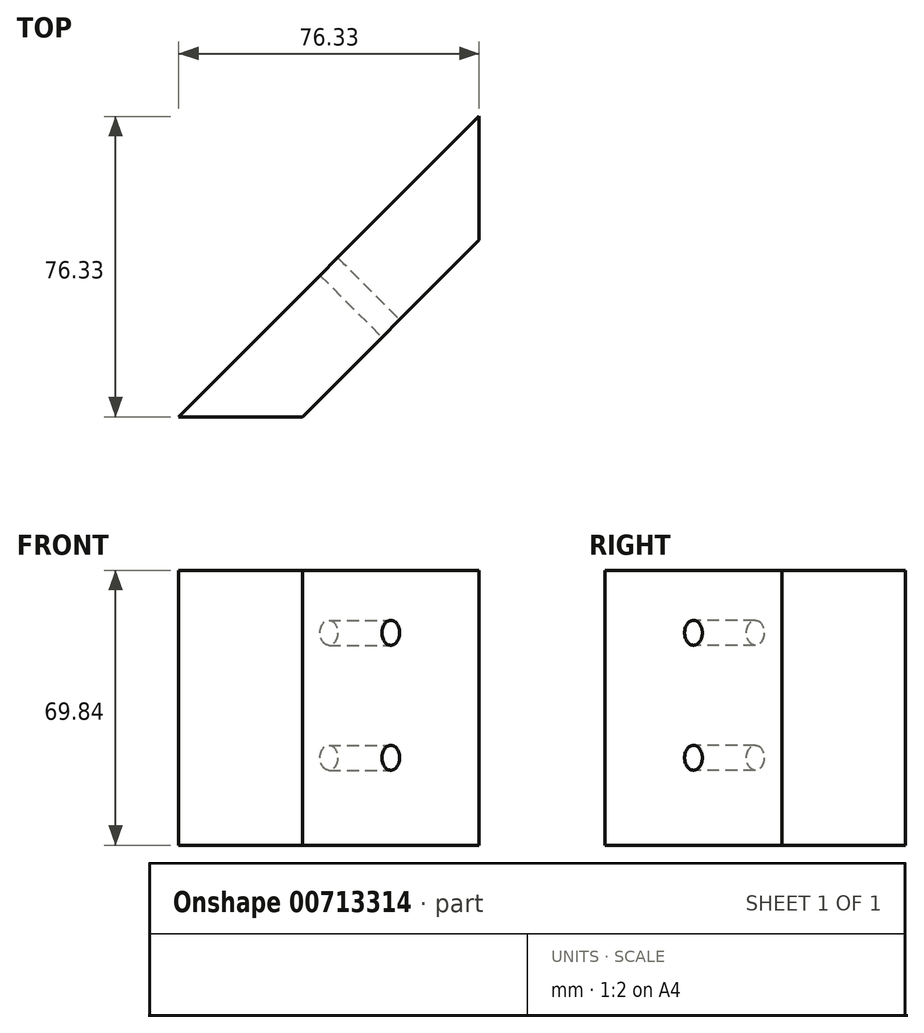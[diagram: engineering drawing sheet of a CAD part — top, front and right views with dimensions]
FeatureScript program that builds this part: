
annotation { "Feature Type Name" : "Feature", "Feature Type Description" : "" }
export const myFeature = defineFeature(function(context is Context, id is Id, definition is map)
    precondition{}
    {
        {
            var Q0;
            Q0=qCreatedBy(makeId("Top.planeOp"),FACE);
            var sketch = newSketch(context, id + "F0", { "sketchPlane" : qUnion([Q0])});
            skLineSegment(sketch, "E0.bottom", {"start": v(-30.3, -46.02) * mm, "end": v(-46.02, -30.3) * mm});
            skLineSegment(sketch, "E0.top", {"start": v(46.02, 30.3) * mm, "end": v(30.3, 46.02) * mm});
            skLineSegment(sketch, "E0.left", {"start": v(-30.3, -46.02) * mm, "end": v(46.02, 30.3) * mm});
            skLineSegment(sketch, "E0.right", {"start": v(-46.02, -30.3) * mm, "end": v(30.3, 46.02) * mm});
            skPoint(sketch, "E0.middle", {"position": v(0, 0) * mm});
            skSolve(sketch);
        }
        {
            var Q0;
            Q0 = qSketchRegion(id + "F0", true);
            extrude(context, id + "F1", {"entities" : qUnion([Q0]), "endBound" : BoundingType.SYMMETRIC, "depth" : 69.85 * mm, "offsetDistance" : 25.4 * mm});
        }
        {
            var Q0;
            Q0=makeQuery(id+"F1.opExtrude","SWEPT_EDGE",EDGE,{"disambiguationData":[OSD([sQuery(id+"F0.wireOp",EDGE,"E0.top"),sQuery(id+"F0.wireOp",EDGE,"E0.left")])]});
            chamfer(context, id + "F2", {"entities" : qUnion([Q0]), "width" : 22.22 * mm, "tangentPropagation" : true});
        }
        {
            var Q0;
            Q0=makeQuery(id+"F1.opExtrude","SWEPT_EDGE",EDGE,{"disambiguationData":[OSD([sQuery(id+"F0.wireOp",EDGE,"E0.bottom"),sQuery(id+"F0.wireOp",EDGE,"E0.left")])]});
            chamfer(context, id + "F3", {"entities" : qUnion([Q0]), "width" : 22.22 * mm, "tangentPropagation" : true});
        }
        {
            var Q0;
            Q0=makeQuery(id+"F1.opExtrude","SWEPT_FACE",FACE,{"disambiguationData":[OSD([sQuery(id+"F0.wireOp",EDGE,"E0.left")])]});
            var sketch = newSketch(context, id + "F4", { "sketchPlane" : qUnion([Q0])});
            skCircle(sketch, "E1", {"center": v(0, 19.05) * mm, "radius": 3.18 * mm});
            skCircle(sketch, "E2", {"center": v(0, -12.7) * mm, "radius": 3.18 * mm});
            skSolve(sketch);
        }
        {
            var Q0;
            Q0=sQuery(id+"F4.wireOp",VERTEX,"E1.center");
            var Q1;
            Q1=makeQuery(id+"F1.opExtrude","SWEPT_BODY",BODY,{"disambiguationData":[OSD([sQuery(id+"F0.wireOp",EDGE,"E0.bottom"),sQuery(id+"F0.wireOp",EDGE,"E0.top"),sQuery(id+"F0.wireOp",EDGE,"E0.left"),sQuery(id+"F0.wireOp",EDGE,"E0.right")])]});
            hole(context, id + "F5", {"style" : HoleStyle.SIMPLE, "endStyle" : HoleEndStyle.THROUGH, "holeDiameter" : 6.35 * mm, "majorDiameter" : 6.35 * mm, "isTappedThrough" : true, "tappedDepth" : 12.7 * mm, "tapClearance" : 3, "locations" : qUnion([Q0]), "scope" : qUnion([Q1])});
        }
        {
            var Q0;
            Q0=sQuery(id+"F4.wireOp",VERTEX,"E2.center");
            var Q1;
            Q1=makeQuery(id+"F1.opExtrude","SWEPT_BODY",BODY,{"disambiguationData":[OSD([sQuery(id+"F0.wireOp",EDGE,"E0.bottom"),sQuery(id+"F0.wireOp",EDGE,"E0.top"),sQuery(id+"F0.wireOp",EDGE,"E0.left"),sQuery(id+"F0.wireOp",EDGE,"E0.right")])]});
            hole(context, id + "F6", {"style" : HoleStyle.SIMPLE, "endStyle" : HoleEndStyle.THROUGH, "holeDiameter" : 6.35 * mm, "majorDiameter" : 6.35 * mm, "isTappedThrough" : true, "tappedDepth" : 12.7 * mm, "tapClearance" : 3, "locations" : qUnion([Q0]), "scope" : qUnion([Q1])});
        }
    });
